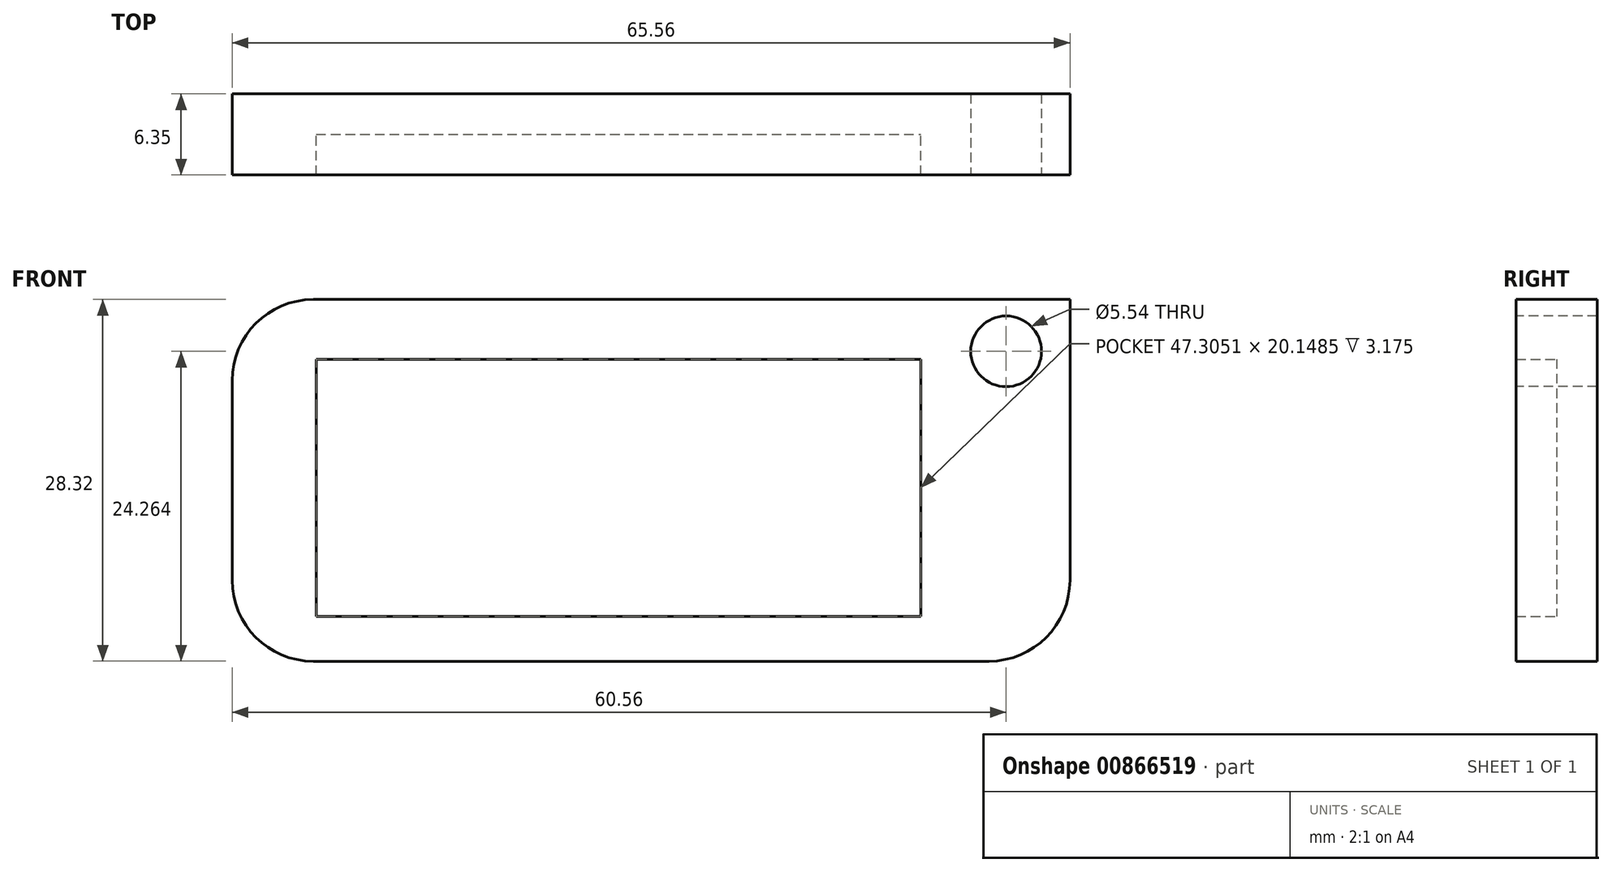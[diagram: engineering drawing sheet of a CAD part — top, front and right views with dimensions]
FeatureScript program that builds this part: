
annotation { "Feature Type Name" : "Feature", "Feature Type Description" : "" }
export const myFeature = defineFeature(function(context is Context, id is Id, definition is map)
    precondition{}
    {
        {
            var Q0;
            Q0=qCreatedBy(makeId("Front.planeOp"),FACE);
            var sketch = newSketch(context, id + "F0", { "sketchPlane" : qUnion([Q0])});
            skLineSegment(sketch, "E0.bottom", {"start": v(6.35, 35.77) * mm, "end": v(65.56, 35.77) * mm});
            skLineSegment(sketch, "E0.top", {"start": v(6.35, 7.45) * mm, "end": v(59.2, 7.45) * mm});
            skLineSegment(sketch, "E0.left", {"start": v(0, 29.42) * mm, "end": v(0, 13.8) * mm});
            skLineSegment(sketch, "E0.right", {"start": v(65.56, 35.77) * mm, "end": v(65.56, 13.8) * mm});
            skLineSegment(sketch, "E1.bottom", {"start": v(6.57, 31.1) * mm, "end": v(53.88, 31.1) * mm});
            skLineSegment(sketch, "E1.top", {"start": v(6.57, 10.95) * mm, "end": v(53.88, 10.95) * mm});
            skLineSegment(sketch, "E1.left", {"start": v(6.57, 31.1) * mm, "end": v(6.57, 10.95) * mm});
            skLineSegment(sketch, "E1.right", {"start": v(53.88, 31.1) * mm, "end": v(53.88, 10.95) * mm});
            skPoint(sketch, "E2.visualSharp", {"position": v(0, 35.77) * mm});
            skArc(sketch, "E2.filletArc", {"start": v(6.35, 35.77) * mm, "mid": v(1.86, 33.91) * mm, "end": v(0, 29.42) * mm});
            skPoint(sketch, "E3.visualSharp", {"position": v(0, 7.45) * mm});
            skArc(sketch, "E3.filletArc", {"start": v(0, 13.8) * mm, "mid": v(1.86, 9.3) * mm, "end": v(6.35, 7.45) * mm});
            skPoint(sketch, "E4.visualSharp", {"position": v(65.56, 7.45) * mm});
            skArc(sketch, "E4.filletArc", {"start": v(59.2, 7.45) * mm, "mid": v(63.7, 9.3) * mm, "end": v(65.56, 13.8) * mm});
            skSolve(sketch);
        }
        {
            var Q0;
            Q0 = qSketchRegion(id + "F0", true);
            extrude(context, id + "F1", {"entities" : qUnion([Q0]), "depth" : 6.35 * mm, "offsetDistance" : 25.4 * mm});
        }
        {
            var Q0;
            Q0=makeQuery(id+"F0.imprint","IMPRINT",FACE,{"disambiguationData":[TD([[makeQuery(id+"F0.imprint","IMPRINT",EDGE,{"derivedFrom":sQuery(id+"F0.wireOp",EDGE,"E1.bottom")}),-1.0]])]});
            extrude(context, id + "F2", {"entities" : qUnion([Q0]), "operationType" : NewBodyOperationType.ADD, "depth" : 3.17 * mm, "offsetDistance" : 25.4 * mm});
        }
        {
            var Q0;
            Q0=makeQuery(id+"F1.opExtrude","CAP_FACE",FACE,{"disambiguationData":[OSD([sQuery(id+"F0.wireOp",EDGE,"E0.bottom"),sQuery(id+"F0.wireOp",EDGE,"E0.top"),sQuery(id+"F0.wireOp",EDGE,"E0.left"),sQuery(id+"F0.wireOp",EDGE,"E0.right"),sQuery(id+"F0.wireOp",EDGE,"E1.bottom"),sQuery(id+"F0.wireOp",EDGE,"E1.top"),sQuery(id+"F0.wireOp",EDGE,"E1.left"),sQuery(id+"F0.wireOp",EDGE,"E1.right"),sQuery(id+"F0.wireOp",EDGE,"E2.filletArc"),sQuery(id+"F0.wireOp",EDGE,"E3.filletArc"),sQuery(id+"F0.wireOp",EDGE,"E4.filletArc")])],"isStart":false});
            var sketch = newSketch(context, id + "F3", { "sketchPlane" : qUnion([Q0])});
            skCircle(sketch, "E5", {"center": v(60.56, 31.71) * mm, "radius": 2.77 * mm});
            skSolve(sketch);
        }
        {
            var Q0;
            Q0 = qSketchRegion(id + "F3", true);
            extrude(context, id + "F4", {"entities" : qUnion([Q0]), "operationType" : NewBodyOperationType.REMOVE, "oppositeDirection" : true, "depth" : 25.4 * mm, "offsetDistance" : 25.4 * mm});
        }
    });
